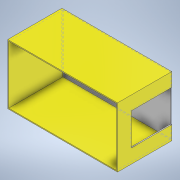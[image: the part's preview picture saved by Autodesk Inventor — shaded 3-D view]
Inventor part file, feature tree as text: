
AUTODESK INVENTOR PART (.ipt)
format: ipt  version: 2022 (Build 260153000, 153)  size: 126,976 bytes
history: native  units: in
note: dims shown in document units (in); Inventor stores cm internally (conversion verified against a paired STEP export)
features: extrude x3, sketch x3
ambient origin geometry x8: Origin, YZ Plane, XZ Plane, XY Plane, X Axis, Y Axis, Z Axis, Center Point
bodies: Solid1 (feature_tree)
feature tree (6):
  extrude  "Extrusion1"  Depth=115.375in
  extrude  "Extrusion2"  Depth=218.688in
  extrude  "Extrusion3"  Depth=108.0in TaperAngle=0.0deg
  sketch  "Sketch1"  dims[d0=214.6875in d1=115.375in]
  sketch  "Sketch2"  dims[d2=1.0in d3=0.0in d4=218.688in]
  sketch  "Sketch3"  dims[d5=119.375in d6=108.0in d7=0.0in d8=80.0in d9=64.0in d10=108.0in d11=0.0in]
